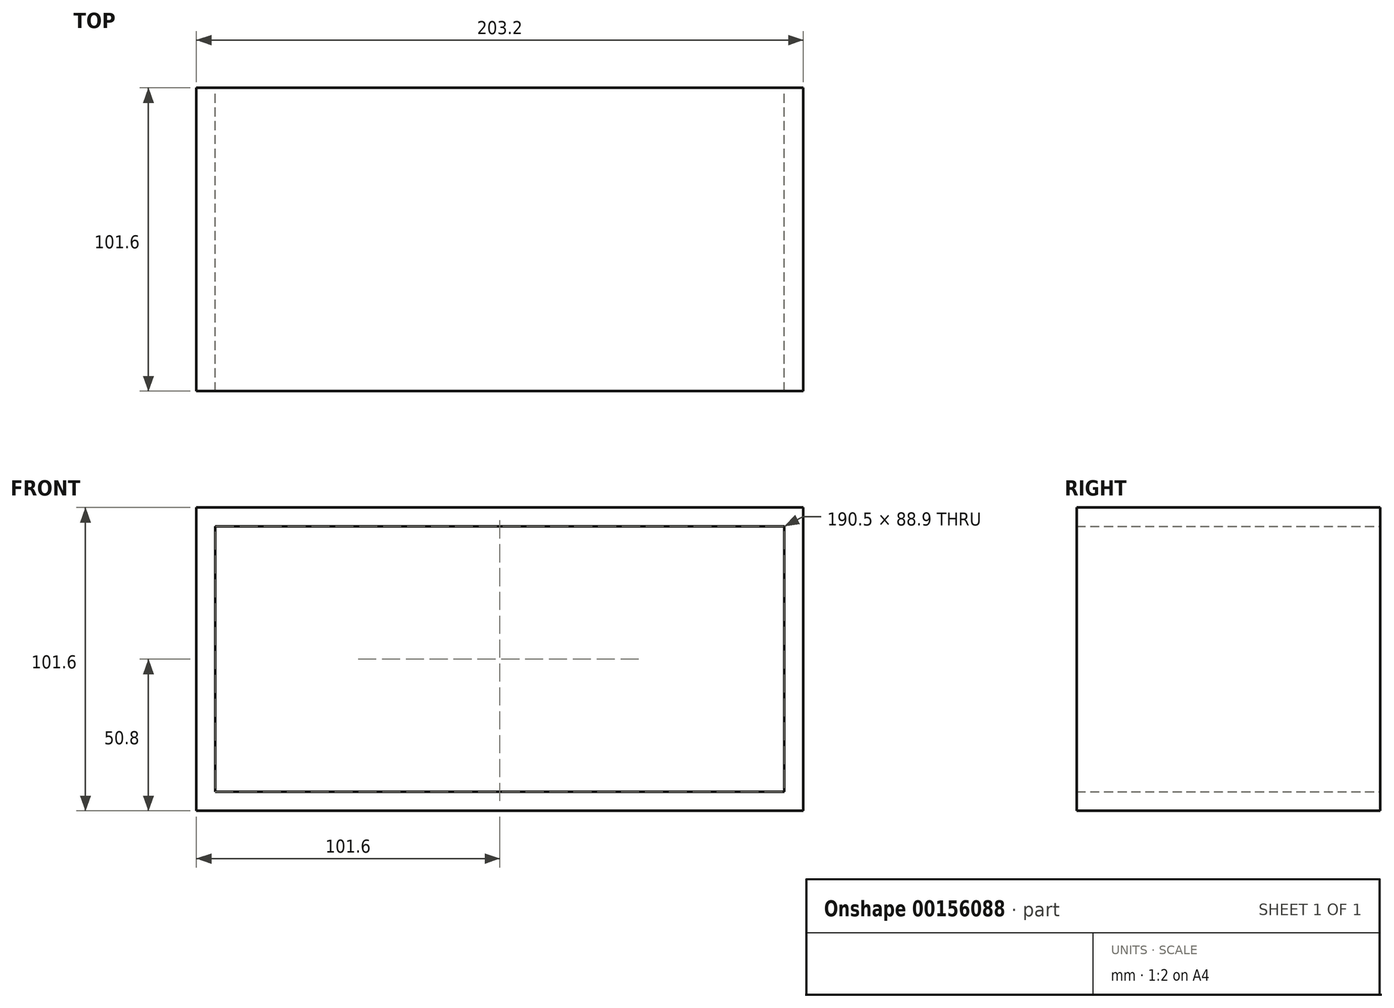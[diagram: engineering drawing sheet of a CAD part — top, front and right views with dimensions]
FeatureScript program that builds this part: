
annotation { "Feature Type Name" : "Feature", "Feature Type Description" : "" }
export const myFeature = defineFeature(function(context is Context, id is Id, definition is map)
    precondition{}
    {
        {
            var Q0;
            Q0=qCreatedBy(makeId("Front.planeOp"),FACE);
            var sketch = newSketch(context, id + "F0", { "sketchPlane" : qUnion([Q0])});
            skLineSegment(sketch, "E0.bottom", {"start": v(101.6, -50.8) * mm, "end": v(-101.6, -50.8) * mm});
            skLineSegment(sketch, "E0.top", {"start": v(101.6, 50.8) * mm, "end": v(-101.6, 50.8) * mm});
            skLineSegment(sketch, "E0.left", {"start": v(101.6, -50.8) * mm, "end": v(101.6, 50.8) * mm});
            skLineSegment(sketch, "E0.right", {"start": v(-101.6, -50.8) * mm, "end": v(-101.6, 50.8) * mm});
            skPoint(sketch, "E0.middle", {"position": v(0, 0) * mm});
            skLineSegment(sketch, "E1.bottom", {"start": v(95.25, 44.45) * mm, "end": v(-95.25, 44.45) * mm});
            skLineSegment(sketch, "E1.top", {"start": v(95.25, -44.45) * mm, "end": v(-95.25, -44.45) * mm});
            skLineSegment(sketch, "E1.left", {"start": v(95.25, 44.45) * mm, "end": v(95.25, -44.45) * mm});
            skLineSegment(sketch, "E1.right", {"start": v(-95.25, 44.45) * mm, "end": v(-95.25, -44.45) * mm});
            skLineSegment(sketch, "E2.bottom", {"start": v(89.35, -38.46) * mm, "end": v(19.5, -38.46) * mm});
            skLineSegment(sketch, "E2.top", {"start": v(89.35, -25.76) * mm, "end": v(19.5, -25.76) * mm});
            skLineSegment(sketch, "E2.left", {"start": v(89.35, -38.46) * mm, "end": v(89.35, -25.76) * mm});
            skLineSegment(sketch, "E2.right", {"start": v(19.5, -38.46) * mm, "end": v(19.5, -25.76) * mm});
            skLineSegment(sketch, "E3.bottom", {"start": v(48.26, -28.9) * mm, "end": v(60.96, -28.9) * mm});
            skLineSegment(sketch, "E3.top", {"start": v(48.26, -35.25) * mm, "end": v(60.96, -35.25) * mm});
            skLineSegment(sketch, "E3.left", {"start": v(48.26, -28.9) * mm, "end": v(48.26, -35.25) * mm});
            skLineSegment(sketch, "E4.bottom", {"start": v(95.25, 44.45) * mm, "end": v(82.55, 44.45) * mm});
            skLineSegment(sketch, "E4.top", {"start": v(95.25, 19.05) * mm, "end": v(82.55, 19.05) * mm});
            skLineSegment(sketch, "E4.left", {"start": v(95.25, 44.45) * mm, "end": v(95.25, 19.05) * mm});
            skLineSegment(sketch, "E4.right", {"start": v(82.55, 44.45) * mm, "end": v(82.55, 19.05) * mm});
            skLineSegment(sketch, "E5", {"start": v(60.96, -28.9) * mm, "end": v(60.96, -35.25) * mm});
            skLineSegment(sketch, "E6.bottom", {"start": v(-95.25, 44.45) * mm, "end": v(0, 44.45) * mm});
            skLineSegment(sketch, "E6.top", {"start": v(-95.25, -44.45) * mm, "end": v(0, -44.45) * mm});
            skLineSegment(sketch, "E6.right", {"start": v(0, 44.45) * mm, "end": v(0, -44.45) * mm});
            skSolve(sketch);
        }
        {
            var Q0;
            Q0=makeQuery(id+"F0.imprint","IMPRINT",FACE,{"disambiguationData":[TD([[makeQuery(id+"F0.imprint","IMPRINT",EDGE,{"derivedFrom":sQuery(id+"F0.wireOp",EDGE,"E0.bottom")}),-1.0]])]});
            extrude(context, id + "F1", {"entities" : qUnion([Q0]), "depth" : 101.6 * mm});
        }
    });
